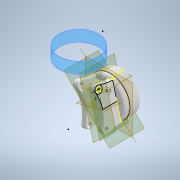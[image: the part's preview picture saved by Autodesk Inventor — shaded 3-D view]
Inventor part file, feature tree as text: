
AUTODESK INVENTOR PART (.ipt)
format: ipt  version: 2022 (Build 260153070, 153G)  size: 325,632 bytes
history: native  units: mm
features: other x7, sketch x6, plane x6, extrude x4, mirror x3, reference x2, fillet x1, loft x1, revolve x1, projected_geometry x1
ambient origin geometry x8: Origin, YZ Plane, XZ Plane, XY Plane, X Axis, Y Axis, Z Axis, Center Point
bodies: Solid1 (feature_tree)
feature tree (32):
  sketch  "Sketch1"  dims[d0=3.0mm d1=7.0mm d2=0.0mm]
  extrude  "Extrusion1"  Depth=7.0mm TaperAngle=0.0deg
  extrude  "Extrusion2"  Depth=2.0mm
  fillet  "Fillet1"  Radius=0.5mm
  plane  "Work Plane1"
  sketch  "Sketch4"  dims[d3=3.0mm d4=0.0mm d5=2.0mm d6=0.5mm]
  extrude  "Extrusion3"  Depth=1.0mm TaperAngle=0.0deg
  sketch  "Sketch6"  dims[d7=1.0mm d9=3.5mm d10=0.0mm]
  plane  "Work Plane2"
  loft  "Loft1"
  mirror  "Mirror2"
  plane  "Work Plane3"
  mirror  "Mirror3"
  plane  "Work Plane5"
  extrude  "Extrusion4"  Depth=10.0mm
  mirror  "Mirror4"
  plane  "Work Plane7"
  revolve  "Revolution1"  [1 undecoded]
  reference  "Reference1"
  reference  "Reference4"
  projected_geometry  "Projected Loop1"
  sketch  "Sketch8"  dims[d11=0.0mm d12=90.0deg d13=0.0mm d14=90.0deg]
  other  "Edges1"
  plane  "Work Plane4"
  sketch  "Sketch9"  dims[d15=10.0mm d16=5.0mm]
  other  "Work Axis1"
  other  "Work Axis3"
  sketch  "Sketch10"  dims[d17=3.0mm d19=1.5mm d20=0.0mm d25=360.0deg d28=2.0mm d29=3.0mm d30=19.52659mm d31=7.652337mm d33=1.091655mm]
  other  "<userpath> laptop\Desktop\sumobotLIDAR\sumobotLIDAR.iam"
  other  "sumobotLIDAR.iam"
  other  "608ZZ bearing:1"
  other  "VL53L1X board:1"
note: 1 required parameter value undecoded (feature->parameter linkage not recoverable at this tier; creation-order binding heuristic only, values carry confidence <= 0.55)
